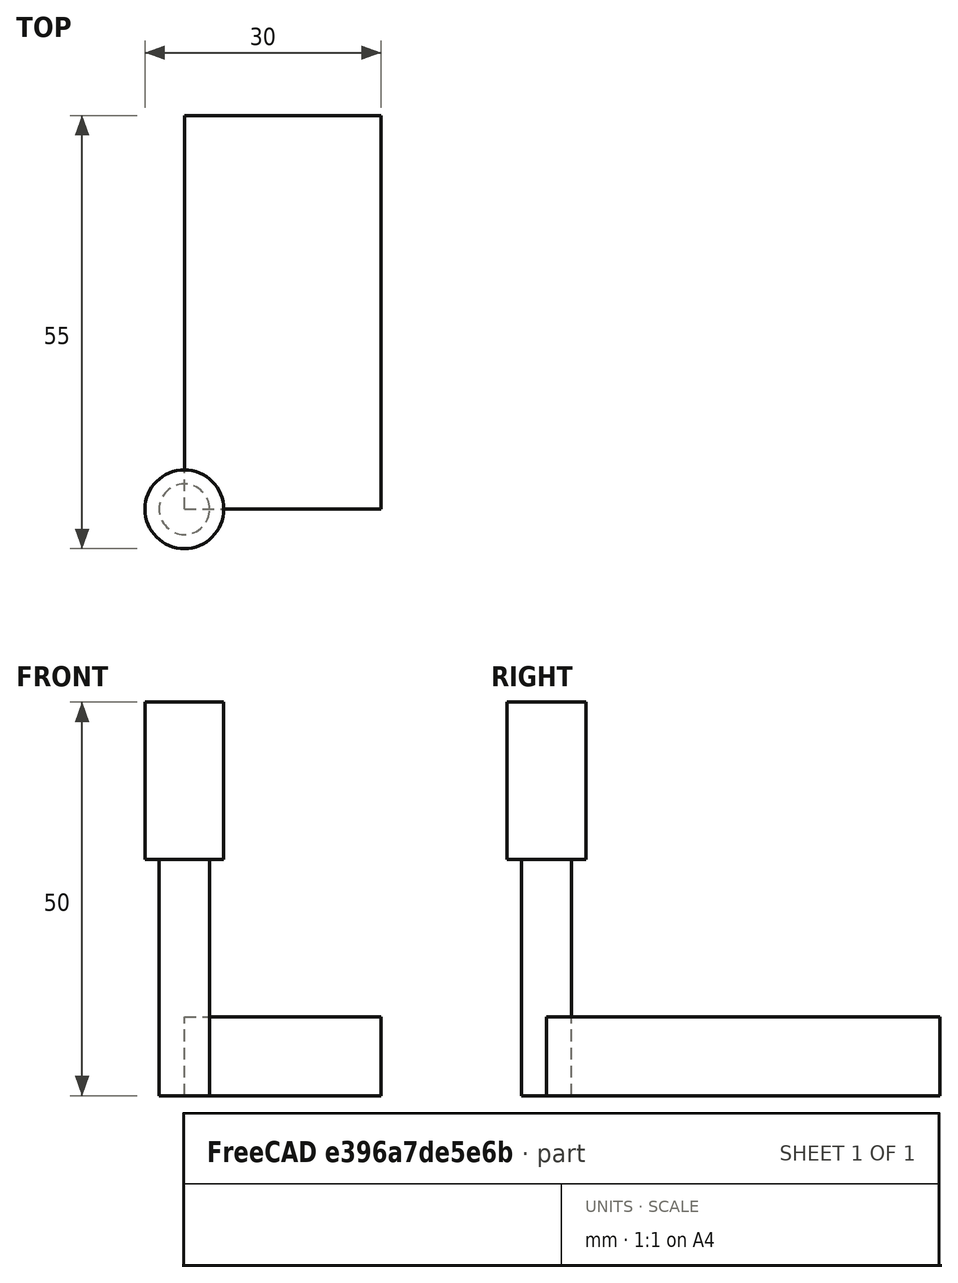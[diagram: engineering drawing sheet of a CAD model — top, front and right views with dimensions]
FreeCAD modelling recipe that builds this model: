
FCSTD DOCUMENT  (FreeCAD 0.19RUnknown)
Label: rectangles
License: All rights reserved
LicenseURL: http://en.wikipedia.org/wiki/All_rights_reserved
objects: Path::FeaturePython×4, Part::FeaturePython×3, App::DocumentObjectGroup×2, Sketcher::SketchObject×1, PartDesign::Pad×1, PartDesign::Body×1, App::FeaturePython×1, Path::FeatureCompoundPython×1, Mesh::FeaturePython×1
note: 8 computed .brp shape members not serialized (recipe doc carries the construction recipe); baked Part::Feature solids carry a one-line shape summary decoded from their .brp

FEATURE [Sketcher::SketchObject] Sketch
  FullyConstrained = true
  MapMode = 5
  Support = -> [XY_Plane]
  sketch-geometry (4):
    g0: LineSegment StartX=0 StartY=50 StartZ=0 EndX=25 EndY=50 EndZ=0
    g1: LineSegment StartX=25 StartY=50 StartZ=0 EndX=25 EndY=0 EndZ=0
    g2: LineSegment StartX=25 StartY=0 StartZ=0 EndX=0 EndY=0 EndZ=0
    g3: LineSegment StartX=0 StartY=0 StartZ=0 EndX=0 EndY=50 EndZ=0
  constraints (11):
    c: Coincident(g0,g1)
    c: Coincident(g1,g2)
    c: Coincident(g2,g3)
    c: Coincident(g3,g0)
    c: Horizontal(g0)
    c: Horizontal(g2)
    c: Vertical(g1)
    c: Vertical(g3)
    c: DistanceX(g0,g0) = 25
    c: Coincident(g2,g-1)
    c: DistanceY(g1,g1) = 50
FEATURE [PartDesign::Pad] Pad
  Direction = (1,1,1)
  Length = 10
  Length2 = 100
  Profile = -> Sketch
  Type = 0
FEATURE [PartDesign::Body] Body
  Group = -> [Sketch,Pad]
  Origin = -> Origin
  Tip = -> Pad
FEATURE [App::FeaturePython] SetupSheet  # Path/CAM operation (typed FeaturePython)
  ClearanceHeightExpression = OpStockZMax+SetupSheet.ClearanceHeightOffset
  ClearanceHeightOffset = 5
  CoolantMode = 0
  CoolantModes = None | Flood | Mist
  FinalDepthExpression = OpFinalDepth
  HorizRapid = 0
  SafeHeightExpression = OpStockZMax+SetupSheet.SafeHeightOffset
  SafeHeightOffset = 3
  StartDepthExpression = OpStartDepth
  StepDownExpression = OpToolDiameter
  VertRapid = 0
FEATURE [Part::FeaturePython] Clone  label="Model-Body"  # Draft clone (typed FeaturePython)
  AttacherType = Attacher::AttachEngine3D
  Fuse = false
  Objects = -> [Body]
  PathResource = Model
  Scale = (1,1,1)
FEATURE [App::DocumentObjectGroup] Model
  Group = -> [Clone]
FEATURE [Part::FeaturePython] Stock001  # WARN: FeaturePython — macro-defined, semantics opaque (R4)
  Height = 10
  Length = 25
  StockType = CreateBox
  Width = 50
FEATURE [Part::FeaturePython] ToolBit001  label="6.4mm Endmill"  # Path/CAM toolbit (typed FeaturePython)
  BitPropertyNames = Chipload | CuttingEdgeHeight | Diameter | Flutes | Length | Material | ShankDiameter
  BitShape = <path>
  Chipload = 0
  CuttingEdgeHeight = 30
  Diameter = 6.4
  File = <userpath>/MensShed/CNCRouter/FreeCAD/Bit/6.4mm_Endmill.fctb
  Flutes = 0
  Length = 50
  Material = 0
  ShankDiameter = 10
  ShapeName = endmill
FEATURE [Path::FeaturePython] __4mm_Endmill  label="6.4mm Endmill001"  # Path/CAM operation (typed FeaturePython)
  HorizFeed = 20
  HorizRapid = 0
  SpindleDir = 0
  SpindleSpeed = 10000
  Tool = -> ToolBit001
  ToolNumber = 2
  VertFeed = 10
  VertRapid = 0
  expr: HorizRapid = SetupSheet.HorizRapid
  expr: VertRapid = SetupSheet.VertRapid
FEATURE [App::DocumentObjectGroup] Tools
  Group = -> [__4mm_Endmill]
FEATURE [Path::FeaturePython] Profile  # Path/CAM operation (typed FeaturePython)
  Active = true
  AreaParams:
    Tolerance = 1e-07
    FitArcs = True
    Simplify = False
    CleanDistance = 0.0
    Accuracy = 0.01
    Unit = 1.0
    MinArcPoints = 4
    MaxArcPoints = 100
    ClipperScale = 10000000.0
    Fill = 0
    Coplanar = 0
    Reorient = True
    Outline = False
    Explode = False
    OpenMode = 0
    Deflection = 0.01
    SubjectFill = 0
    ClipFill = 0
    Offset = 3.2
    ExtraPass = 0
    Stepover = 0.0
    LastStepover = 0.0
    JoinType = 0
    EndType = 0
    MiterLimit = 2.0
    RoundPrecision = 0.0
    PocketMode = 0
    ToolRadius = 1.0
    PocketExtraOffset = 0.0
    PocketStepover = 0.0
    PocketLastStepover = 0.0
    FromCenter = False
    Angle = 45.0
    AngleShift = 0.0
    Shift = 0.0
    Thicken = False
    SectionCount = -1
    Stepdown = 1.0
    SectionOffset = 0.0
    SectionTolerance = 1e-06
    SectionMode = 2
    Project = False
  AttemptInverseAngle = true
  ClearanceHeight = 15
  CoolantMode = None
  CycleTime = 00:00:24
  Direction = 0
  EnableRotation = 0
  FinalDepth = 0
  HandleMultipleFeatures = 0
  InverseAngle = false
  JoinType = 0
  LimitDepthToFace = true
  MiterLimit = 0.1
  OffsetExtra = 0
  OpFinalDepth = 0
  OpStartDepth = 10
  OpStockZMax = 10
  OpStockZMin = 0
  OpToolDiameter = 6.4
  PathParams = {'orientation': 1, 'feedrate': 20.0, 'feedrate_v': 10.0, 'verbose': True, 'resume_height': 13.0, 'retraction': 15.0, 'return_end': True, 'preamble': False}
  ReverseDirection = false
  SafeHeight = 13
  Side = 0
  StartDepth = 10
  StartPoint = (0,0,0)
  StepDown = 6.4
  ToolController = -> __4mm_Endmill
  UseComp = true
  UseStartPoint = false
  processCircles = false
  processHoles = false
  processPerimeter = true
  expr: ClearanceHeight = OpStockZMax + SetupSheet.ClearanceHeightOffset
  expr: SafeHeight = OpStockZMax + SetupSheet.SafeHeightOffset
  expr: StepDown = OpToolDiameter
  expr: FinalDepth = OpFinalDepth
  expr: StartDepth = OpStartDepth
FEATURE [Path::FeaturePython] Array  # Path/CAM operation (typed FeaturePython)
  Angle = 0
  Base = -> Profile
  Centre = (0,0,0)
  Copies = 5
  CopiesX = 5
  CopiesY = 5
  Offset = (35,60,0)
  ToolController = -> __4mm_Endmill
  Type = 1
FEATURE [Path::FeatureCompoundPython] Operations  # Path/CAM operation (typed FeaturePython)
  Group = -> [Profile,Array]
  UsePlacements = false
FEATURE [Path::FeaturePython] Job  # Path/CAM operation (typed FeaturePython)
  CycleTime = 00:00:48
  Fixtures = G54
  GeometryTolerance = 0.01
  Model = -> Model
  Operations = -> Operations
  OrderOutputBy = 0
  PostProcessor = 7
  PostProcessorOutputFile = %D/%d.ngc
  SetupSheet = -> SetupSheet
  SplitOutput = false
  Stock = -> Stock001
  Tools = -> Tools
FEATURE [Mesh::FeaturePython] CutMaterial  # WARN: FeaturePython — macro-defined, semantics opaque (R4)
note: 1 file-system path scrubbed to <path> (originals preserved in the JSON sidecar)
